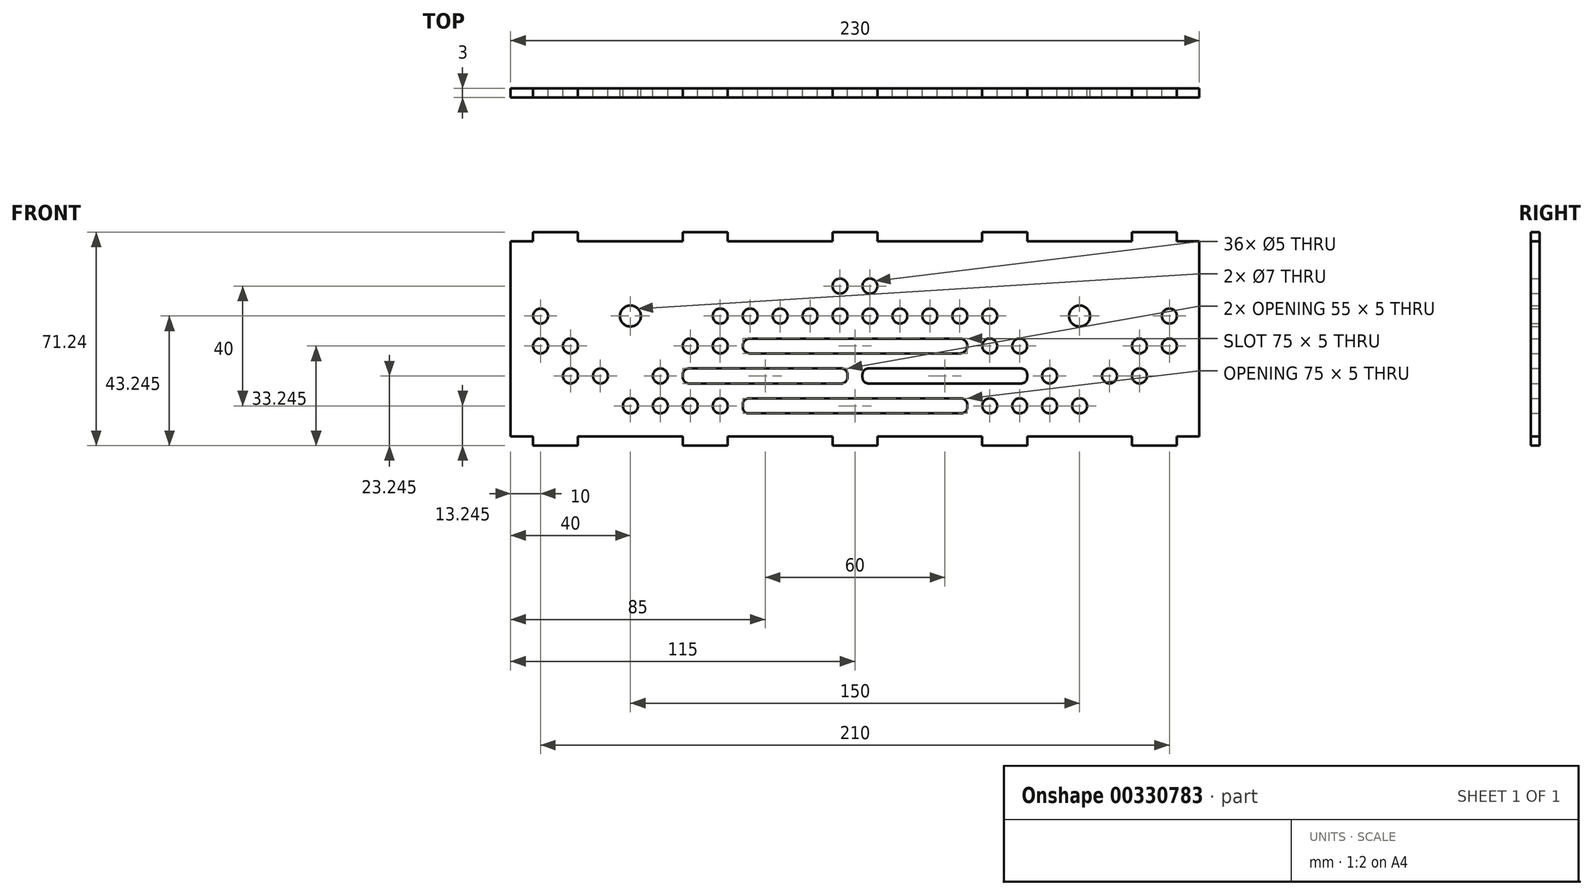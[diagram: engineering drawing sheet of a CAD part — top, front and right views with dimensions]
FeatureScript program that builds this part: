
annotation { "Feature Type Name" : "Feature", "Feature Type Description" : "" }
export const myFeature = defineFeature(function(context is Context, id is Id, definition is map)
    precondition{}
    {
        {
            var Q0;
            Q0=qCreatedBy(makeId("Front.planeOp"),FACE);
            var sketch = newSketch(context, id + "F0", { "sketchPlane" : qUnion([Q0])});
            skLineSegment(sketch, "E0.bottom", {"start": v(115, -32.62) * mm, "end": v(-115, -32.63) * mm});
            skLineSegment(sketch, "E0.top", {"start": v(115, 32.63) * mm, "end": v(-115, 32.62) * mm});
            skLineSegment(sketch, "E0.left", {"start": v(115, -32.62) * mm, "end": v(115, 32.63) * mm});
            skLineSegment(sketch, "E0.right", {"start": v(-115, -32.63) * mm, "end": v(-115, 32.62) * mm});
            skPoint(sketch, "E0.middle", {"position": v(0, 0) * mm});
            skLineSegment(sketch, "E1.bottom", {"start": v(-107.5, -32.63) * mm, "end": v(-92.5, -32.63) * mm});
            skLineSegment(sketch, "E1.top", {"start": v(-107.5, -35.63) * mm, "end": v(-92.5, -35.63) * mm});
            skLineSegment(sketch, "E1.left", {"start": v(-107.5, -32.63) * mm, "end": v(-107.5, -35.63) * mm});
            skLineSegment(sketch, "E1.right", {"start": v(-92.5, -32.63) * mm, "end": v(-92.5, -35.63) * mm});
            skLineSegment(sketch, "E2.1.0.0", {"start": v(-57.5, -32.63) * mm, "end": v(-57.5, -35.63) * mm});
            skLineSegment(sketch, "E2.1.0.1", {"start": v(-57.5, -32.62) * mm, "end": v(-42.5, -32.62) * mm});
            skLineSegment(sketch, "E2.1.0.2", {"start": v(-42.5, -32.63) * mm, "end": v(-42.5, -35.63) * mm});
            skLineSegment(sketch, "E2.1.0.3", {"start": v(-57.5, -35.63) * mm, "end": v(-42.5, -35.63) * mm});
            skLineSegment(sketch, "E2.2.0.0", {"start": v(-7.5, -32.63) * mm, "end": v(-7.5, -35.63) * mm});
            skLineSegment(sketch, "E2.2.0.1", {"start": v(-7.5, -32.62) * mm, "end": v(7.5, -32.62) * mm});
            skLineSegment(sketch, "E2.2.0.2", {"start": v(7.5, -32.63) * mm, "end": v(7.5, -35.63) * mm});
            skLineSegment(sketch, "E2.2.0.3", {"start": v(-7.5, -35.62) * mm, "end": v(7.5, -35.62) * mm});
            skLineSegment(sketch, "E2.3.0.0", {"start": v(42.5, -32.63) * mm, "end": v(42.5, -35.63) * mm});
            skLineSegment(sketch, "E2.3.0.1", {"start": v(42.5, -32.62) * mm, "end": v(57.5, -32.62) * mm});
            skLineSegment(sketch, "E2.3.0.2", {"start": v(57.5, -32.63) * mm, "end": v(57.5, -35.63) * mm});
            skLineSegment(sketch, "E2.3.0.3", {"start": v(42.5, -35.62) * mm, "end": v(57.5, -35.62) * mm});
            skLineSegment(sketch, "E2.4.0.0", {"start": v(92.5, -32.63) * mm, "end": v(92.5, -35.63) * mm});
            skLineSegment(sketch, "E2.4.0.1", {"start": v(92.5, -32.62) * mm, "end": v(107.5, -32.62) * mm});
            skLineSegment(sketch, "E2.4.0.2", {"start": v(107.5, -32.63) * mm, "end": v(107.5, -35.63) * mm});
            skLineSegment(sketch, "E2.4.0.3", {"start": v(92.5, -35.62) * mm, "end": v(107.5, -35.62) * mm});
            skLineSegment(sketch, "E2.direction1", {"start": v(-107.5, -35.63) * mm, "end": v(-57.5, -35.63) * mm, "construction": true});
            skCircle(sketch, "E3.0.2.0", {"center": v(-105, -2.38) * mm, "radius": 2.5 * mm});
            skCircle(sketch, "E3.0.3.0", {"center": v(-105, 7.62) * mm, "radius": 2.5 * mm});
            skCircle(sketch, "E3.1.1.0", {"center": v(-95, -12.38) * mm, "radius": 2.5 * mm});
            skCircle(sketch, "E3.1.2.0", {"center": v(-95, -2.38) * mm, "radius": 2.5 * mm});
            skCircle(sketch, "E3.2.1.0", {"center": v(-85, -12.38) * mm, "radius": 2.5 * mm});
            skCircle(sketch, "E3.3.0.0", {"center": v(-75, -22.38) * mm, "radius": 2.5 * mm});
            skCircle(sketch, "E3.3.3.0", {"center": v(-75, 7.62) * mm, "radius": 2.5 * mm});
            skCircle(sketch, "E3.4.0.0", {"center": v(-65, -22.38) * mm, "radius": 2.5 * mm});
            skCircle(sketch, "E3.4.1.0", {"center": v(-65, -12.38) * mm, "radius": 2.5 * mm});
            skCircle(sketch, "E3.5.0.0", {"center": v(-55, -22.38) * mm, "radius": 2.5 * mm});
            skCircle(sketch, "E3.5.1.0", {"center": v(-55, -12.38) * mm, "radius": 2.5 * mm});
            skCircle(sketch, "E3.5.2.0", {"center": v(-55, -2.38) * mm, "radius": 2.5 * mm});
            skCircle(sketch, "E3.6.0.0", {"center": v(-45, -22.38) * mm, "radius": 2.5 * mm});
            skCircle(sketch, "E3.6.1.0", {"center": v(-45, -12.38) * mm, "radius": 2.5 * mm});
            skCircle(sketch, "E3.6.2.0", {"center": v(-45, -2.38) * mm, "radius": 2.5 * mm});
            skCircle(sketch, "E3.6.3.0", {"center": v(-45, 7.62) * mm, "radius": 2.5 * mm});
            skCircle(sketch, "E3.7.0.0", {"center": v(-35, -22.38) * mm, "radius": 2.5 * mm});
            skCircle(sketch, "E3.7.1.0", {"center": v(-35, -12.38) * mm, "radius": 2.5 * mm});
            skCircle(sketch, "E3.7.2.0", {"center": v(-35, -2.38) * mm, "radius": 2.5 * mm});
            skCircle(sketch, "E3.7.3.0", {"center": v(-35, 7.62) * mm, "radius": 2.5 * mm});
            skCircle(sketch, "E3.8.0.0", {"center": v(-25, -22.38) * mm, "radius": 2.5 * mm});
            skCircle(sketch, "E3.8.1.0", {"center": v(-25, -12.38) * mm, "radius": 2.5 * mm});
            skCircle(sketch, "E3.8.2.0", {"center": v(-25, -2.38) * mm, "radius": 2.5 * mm});
            skCircle(sketch, "E3.8.3.0", {"center": v(-25, 7.62) * mm, "radius": 2.5 * mm});
            skCircle(sketch, "E3.9.0.0", {"center": v(-15, -22.38) * mm, "radius": 2.5 * mm});
            skCircle(sketch, "E3.9.1.0", {"center": v(-15, -12.38) * mm, "radius": 2.5 * mm});
            skCircle(sketch, "E3.9.2.0", {"center": v(-15, -2.38) * mm, "radius": 2.5 * mm});
            skCircle(sketch, "E3.9.3.0", {"center": v(-15, 7.62) * mm, "radius": 2.5 * mm});
            skCircle(sketch, "E3.10.0.0", {"center": v(-5, -22.38) * mm, "radius": 2.5 * mm});
            skCircle(sketch, "E3.10.1.0", {"center": v(-5, -12.38) * mm, "radius": 2.5 * mm});
            skCircle(sketch, "E3.10.2.0", {"center": v(-5, -2.38) * mm, "radius": 2.5 * mm});
            skCircle(sketch, "E3.10.3.0", {"center": v(-5, 7.62) * mm, "radius": 2.5 * mm});
            skCircle(sketch, "E3.11.0.0", {"center": v(5, -22.38) * mm, "radius": 2.5 * mm});
            skCircle(sketch, "E3.11.1.0", {"center": v(5, -12.38) * mm, "radius": 2.5 * mm});
            skCircle(sketch, "E3.11.2.0", {"center": v(5, -2.38) * mm, "radius": 2.5 * mm});
            skCircle(sketch, "E3.11.3.0", {"center": v(5, 7.62) * mm, "radius": 2.5 * mm});
            skCircle(sketch, "E3.12.0.0", {"center": v(15, -22.38) * mm, "radius": 2.5 * mm});
            skCircle(sketch, "E3.12.1.0", {"center": v(15, -12.38) * mm, "radius": 2.5 * mm});
            skCircle(sketch, "E3.12.2.0", {"center": v(15, -2.38) * mm, "radius": 2.5 * mm});
            skCircle(sketch, "E3.12.3.0", {"center": v(15, 7.62) * mm, "radius": 2.5 * mm});
            skCircle(sketch, "E3.13.0.0", {"center": v(25, -22.38) * mm, "radius": 2.5 * mm});
            skCircle(sketch, "E3.13.1.0", {"center": v(25, -12.38) * mm, "radius": 2.5 * mm});
            skCircle(sketch, "E3.13.2.0", {"center": v(25, -2.38) * mm, "radius": 2.5 * mm});
            skCircle(sketch, "E3.13.3.0", {"center": v(25, 7.62) * mm, "radius": 2.5 * mm});
            skCircle(sketch, "E3.14.0.0", {"center": v(35, -22.38) * mm, "radius": 2.5 * mm});
            skCircle(sketch, "E3.14.1.0", {"center": v(35, -12.38) * mm, "radius": 2.5 * mm});
            skCircle(sketch, "E3.14.2.0", {"center": v(35, -2.38) * mm, "radius": 2.5 * mm});
            skCircle(sketch, "E3.14.3.0", {"center": v(35, 7.62) * mm, "radius": 2.5 * mm});
            skCircle(sketch, "E3.15.0.0", {"center": v(45, -22.38) * mm, "radius": 2.5 * mm});
            skCircle(sketch, "E3.15.1.0", {"center": v(45, -12.38) * mm, "radius": 2.5 * mm});
            skCircle(sketch, "E3.15.2.0", {"center": v(45, -2.38) * mm, "radius": 2.5 * mm});
            skCircle(sketch, "E3.15.3.0", {"center": v(45, 7.62) * mm, "radius": 2.5 * mm});
            skCircle(sketch, "E3.16.0.0", {"center": v(55, -22.38) * mm, "radius": 2.5 * mm});
            skCircle(sketch, "E3.16.1.0", {"center": v(55, -12.38) * mm, "radius": 2.5 * mm});
            skCircle(sketch, "E3.16.2.0", {"center": v(55, -2.38) * mm, "radius": 2.5 * mm});
            skCircle(sketch, "E3.17.0.0", {"center": v(65, -22.38) * mm, "radius": 2.5 * mm});
            skCircle(sketch, "E3.17.1.0", {"center": v(65, -12.38) * mm, "radius": 2.5 * mm});
            skCircle(sketch, "E3.18.0.0", {"center": v(75, -22.38) * mm, "radius": 2.5 * mm});
            skCircle(sketch, "E3.18.3.0", {"center": v(75, 7.62) * mm, "radius": 2.5 * mm});
            skCircle(sketch, "E3.19.1.0", {"center": v(85, -12.38) * mm, "radius": 2.5 * mm});
            skCircle(sketch, "E3.20.1.0", {"center": v(95, -12.38) * mm, "radius": 2.5 * mm});
            skCircle(sketch, "E3.20.2.0", {"center": v(95, -2.38) * mm, "radius": 2.5 * mm});
            skCircle(sketch, "E3.21.2.0", {"center": v(105, -2.38) * mm, "radius": 2.5 * mm});
            skCircle(sketch, "E3.21.3.0", {"center": v(105, 7.62) * mm, "radius": 2.5 * mm});
            skLineSegment(sketch, "E4.bottom", {"start": v(-107.5, 32.62) * mm, "end": v(-92.5, 32.62) * mm});
            skLineSegment(sketch, "E4.top", {"start": v(-107.5, 35.63) * mm, "end": v(-92.5, 35.63) * mm});
            skLineSegment(sketch, "E4.left", {"start": v(-107.5, 32.62) * mm, "end": v(-107.5, 35.63) * mm});
            skLineSegment(sketch, "E4.right", {"start": v(-92.5, 32.62) * mm, "end": v(-92.5, 35.63) * mm});
            skLineSegment(sketch, "E5.1.0.0", {"start": v(-57.5, 32.62) * mm, "end": v(-57.5, 35.63) * mm});
            skLineSegment(sketch, "E5.1.0.1", {"start": v(-57.5, 35.63) * mm, "end": v(-42.5, 35.63) * mm});
            skLineSegment(sketch, "E5.1.0.2", {"start": v(-42.5, 32.62) * mm, "end": v(-42.5, 35.63) * mm});
            skLineSegment(sketch, "E5.1.0.3", {"start": v(-57.5, 32.62) * mm, "end": v(-42.5, 32.62) * mm});
            skLineSegment(sketch, "E5.2.0.0", {"start": v(-7.5, 32.62) * mm, "end": v(-7.5, 35.63) * mm});
            skLineSegment(sketch, "E5.2.0.1", {"start": v(-7.5, 35.63) * mm, "end": v(7.5, 35.63) * mm});
            skLineSegment(sketch, "E5.2.0.2", {"start": v(7.5, 32.62) * mm, "end": v(7.5, 35.63) * mm});
            skLineSegment(sketch, "E5.2.0.3", {"start": v(-7.5, 32.62) * mm, "end": v(7.5, 32.62) * mm});
            skLineSegment(sketch, "E5.3.0.0", {"start": v(42.5, 32.62) * mm, "end": v(42.5, 35.63) * mm});
            skLineSegment(sketch, "E5.3.0.1", {"start": v(42.5, 35.63) * mm, "end": v(57.5, 35.63) * mm});
            skLineSegment(sketch, "E5.3.0.2", {"start": v(57.5, 32.62) * mm, "end": v(57.5, 35.63) * mm});
            skLineSegment(sketch, "E5.3.0.3", {"start": v(42.5, 32.62) * mm, "end": v(57.5, 32.62) * mm});
            skLineSegment(sketch, "E5.4.0.0", {"start": v(92.5, 32.62) * mm, "end": v(92.5, 35.63) * mm});
            skLineSegment(sketch, "E5.4.0.1", {"start": v(92.5, 35.63) * mm, "end": v(107.5, 35.63) * mm});
            skLineSegment(sketch, "E5.4.0.2", {"start": v(107.5, 32.62) * mm, "end": v(107.5, 35.63) * mm});
            skLineSegment(sketch, "E5.4.0.3", {"start": v(92.5, 32.62) * mm, "end": v(107.5, 32.62) * mm});
            skLineSegment(sketch, "E5.direction1", {"start": v(-107.5, 32.62) * mm, "end": v(-57.5, 32.62) * mm, "construction": true});
            skCircle(sketch, "E6", {"center": v(-75, 7.62) * mm, "radius": 3.5 * mm});
            skCircle(sketch, "E7", {"center": v(75, 7.63) * mm, "radius": 3.5 * mm});
            skLineSegment(sketch, "E8.bottom", {"start": v(4.5, -9.88) * mm, "end": v(55.5, -9.88) * mm});
            skLineSegment(sketch, "E8.top", {"start": v(4.5, -14.88) * mm, "end": v(55.5, -14.88) * mm});
            skLineSegment(sketch, "E8.left", {"start": v(2.5, -11.88) * mm, "end": v(2.5, -12.88) * mm});
            skLineSegment(sketch, "E8.right", {"start": v(57.5, -11.88) * mm, "end": v(57.5, -12.88) * mm});
            skPoint(sketch, "E9.visualSharp", {"position": v(2.5, -9.88) * mm});
            skArc(sketch, "E9.filletArc", {"start": v(4.5, -9.88) * mm, "mid": v(3.09, -10.46) * mm, "end": v(2.5, -11.88) * mm});
            skPoint(sketch, "E10.visualSharp", {"position": v(2.5, -14.88) * mm});
            skArc(sketch, "E10.filletArc", {"start": v(2.5, -12.88) * mm, "mid": v(3.09, -14.29) * mm, "end": v(4.5, -14.88) * mm});
            skPoint(sketch, "E11.visualSharp", {"position": v(57.5, -14.88) * mm});
            skArc(sketch, "E11.filletArc", {"start": v(55.5, -14.88) * mm, "mid": v(56.91, -14.29) * mm, "end": v(57.5, -12.88) * mm});
            skPoint(sketch, "E12.visualSharp", {"position": v(57.5, -9.88) * mm});
            skArc(sketch, "E12.filletArc", {"start": v(57.5, -11.88) * mm, "mid": v(56.91, -10.46) * mm, "end": v(55.5, -9.88) * mm});
            skLineSegment(sketch, "E13.bottom", {"start": v(-35.5, -19.88) * mm, "end": v(35.5, -19.88) * mm});
            skLineSegment(sketch, "E13.top", {"start": v(-35.5, -24.88) * mm, "end": v(35.5, -24.88) * mm});
            skLineSegment(sketch, "E13.left", {"start": v(-37.5, -21.88) * mm, "end": v(-37.5, -22.88) * mm});
            skLineSegment(sketch, "E13.right", {"start": v(37.5, -21.88) * mm, "end": v(37.5, -22.88) * mm});
            skPoint(sketch, "E14.visualSharp", {"position": v(-37.5, -19.88) * mm});
            skArc(sketch, "E14.filletArc", {"start": v(-35.5, -19.88) * mm, "mid": v(-36.91, -20.46) * mm, "end": v(-37.5, -21.88) * mm});
            skPoint(sketch, "E15.visualSharp", {"position": v(-37.5, -24.88) * mm});
            skArc(sketch, "E15.filletArc", {"start": v(-37.5, -22.88) * mm, "mid": v(-36.91, -24.29) * mm, "end": v(-35.5, -24.88) * mm});
            skPoint(sketch, "E16.visualSharp", {"position": v(37.5, -24.88) * mm});
            skArc(sketch, "E16.filletArc", {"start": v(35.5, -24.88) * mm, "mid": v(36.91, -24.29) * mm, "end": v(37.5, -22.88) * mm});
            skPoint(sketch, "E17.visualSharp", {"position": v(37.5, -19.88) * mm});
            skArc(sketch, "E17.filletArc", {"start": v(37.5, -21.88) * mm, "mid": v(36.91, -20.46) * mm, "end": v(35.5, -19.88) * mm});
            skLineSegment(sketch, "E18.bottom", {"start": v(-55.5, -9.88) * mm, "end": v(-4.5, -9.88) * mm});
            skLineSegment(sketch, "E18.top", {"start": v(-55.5, -14.88) * mm, "end": v(-4.5, -14.88) * mm});
            skLineSegment(sketch, "E18.left", {"start": v(-57.5, -11.88) * mm, "end": v(-57.5, -12.88) * mm});
            skLineSegment(sketch, "E18.right", {"start": v(-2.5, -11.88) * mm, "end": v(-2.5, -12.88) * mm});
            skPoint(sketch, "E19.visualSharp", {"position": v(-57.5, -9.88) * mm});
            skArc(sketch, "E19.filletArc", {"start": v(-55.5, -9.88) * mm, "mid": v(-56.91, -10.46) * mm, "end": v(-57.5, -11.88) * mm});
            skPoint(sketch, "E20.visualSharp", {"position": v(-57.5, -14.88) * mm});
            skArc(sketch, "E20.filletArc", {"start": v(-57.5, -12.88) * mm, "mid": v(-56.91, -14.29) * mm, "end": v(-55.5, -14.88) * mm});
            skPoint(sketch, "E21.visualSharp", {"position": v(-2.5, -14.88) * mm});
            skArc(sketch, "E21.filletArc", {"start": v(-4.5, -14.88) * mm, "mid": v(-3.09, -14.29) * mm, "end": v(-2.5, -12.88) * mm});
            skPoint(sketch, "E22.visualSharp", {"position": v(-2.5, -9.88) * mm});
            skArc(sketch, "E22.filletArc", {"start": v(-2.5, -11.88) * mm, "mid": v(-3.09, -10.46) * mm, "end": v(-4.5, -9.88) * mm});
            skCircle(sketch, "E23", {"center": v(-5, 17.62) * mm, "radius": 2.5 * mm});
            skCircle(sketch, "E24", {"center": v(5, 17.62) * mm, "radius": 2.5 * mm});
            skLineSegment(sketch, "E25.bottom", {"start": v(35, -4.88) * mm, "end": v(-35, -4.88) * mm});
            skLineSegment(sketch, "E25.top", {"start": v(35, 0.12) * mm, "end": v(-35, 0.12) * mm});
            skLineSegment(sketch, "E25.left", {"start": v(35, -4.88) * mm, "end": v(35, 0.12) * mm});
            skLineSegment(sketch, "E25.right", {"start": v(-35, -4.88) * mm, "end": v(-35, 0.12) * mm});
            skPoint(sketch, "E25.middle", {"position": v(0, -2.38) * mm});
            skSolve(sketch);
        }
        {
            var Q0;
            Q0 = qSketchRegion(id + "F0", true);
            extrude(context, id + "F1", {"entities" : qUnion([Q0]), "depth" : 3 * mm});
        }
    });
